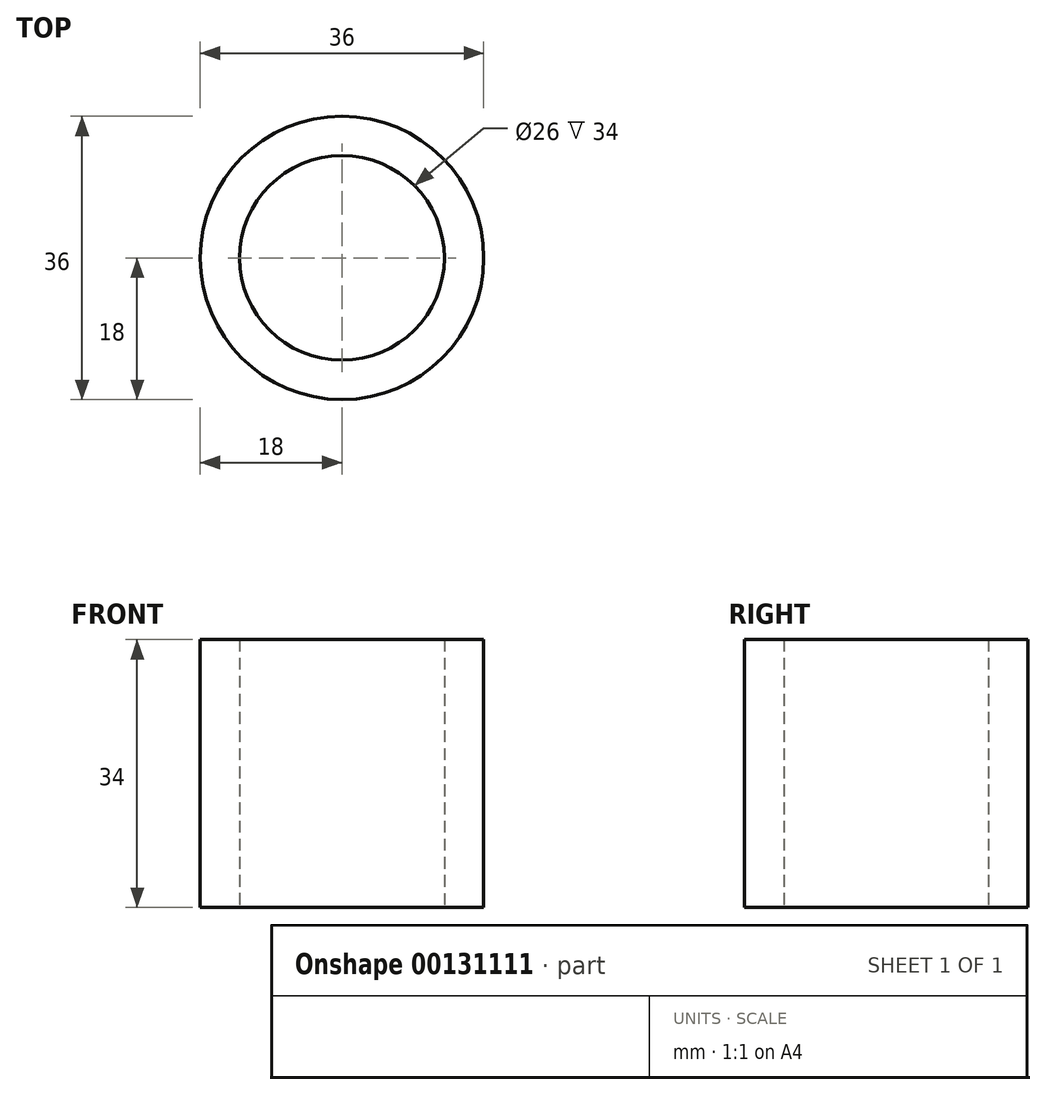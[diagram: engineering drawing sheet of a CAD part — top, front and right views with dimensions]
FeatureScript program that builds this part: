
annotation { "Feature Type Name" : "Feature", "Feature Type Description" : "" }
export const myFeature = defineFeature(function(context is Context, id is Id, definition is map)
    precondition{}
    {
        {
            var Q0;
            Q0=qCreatedBy(makeId("Top.planeOp"),FACE);
            var sketch = newSketch(context, id + "F0", { "sketchPlane" : qUnion([Q0])});
            skCircle(sketch, "E0", {"center": v(0, 0) * mm, "radius": 18 * mm});
            skCircle(sketch, "E1", {"center": v(0, 0) * mm, "radius": 13 * mm});
            skSolve(sketch);
        }
        {
            var Q0;
            Q0 = qSketchRegion(id + "F0", true);
            extrude(context, id + "F1", {"entities" : qUnion([Q0]), "endBound" : BoundingType.SYMMETRIC, "depth" : 34 * mm});
        }
    });
